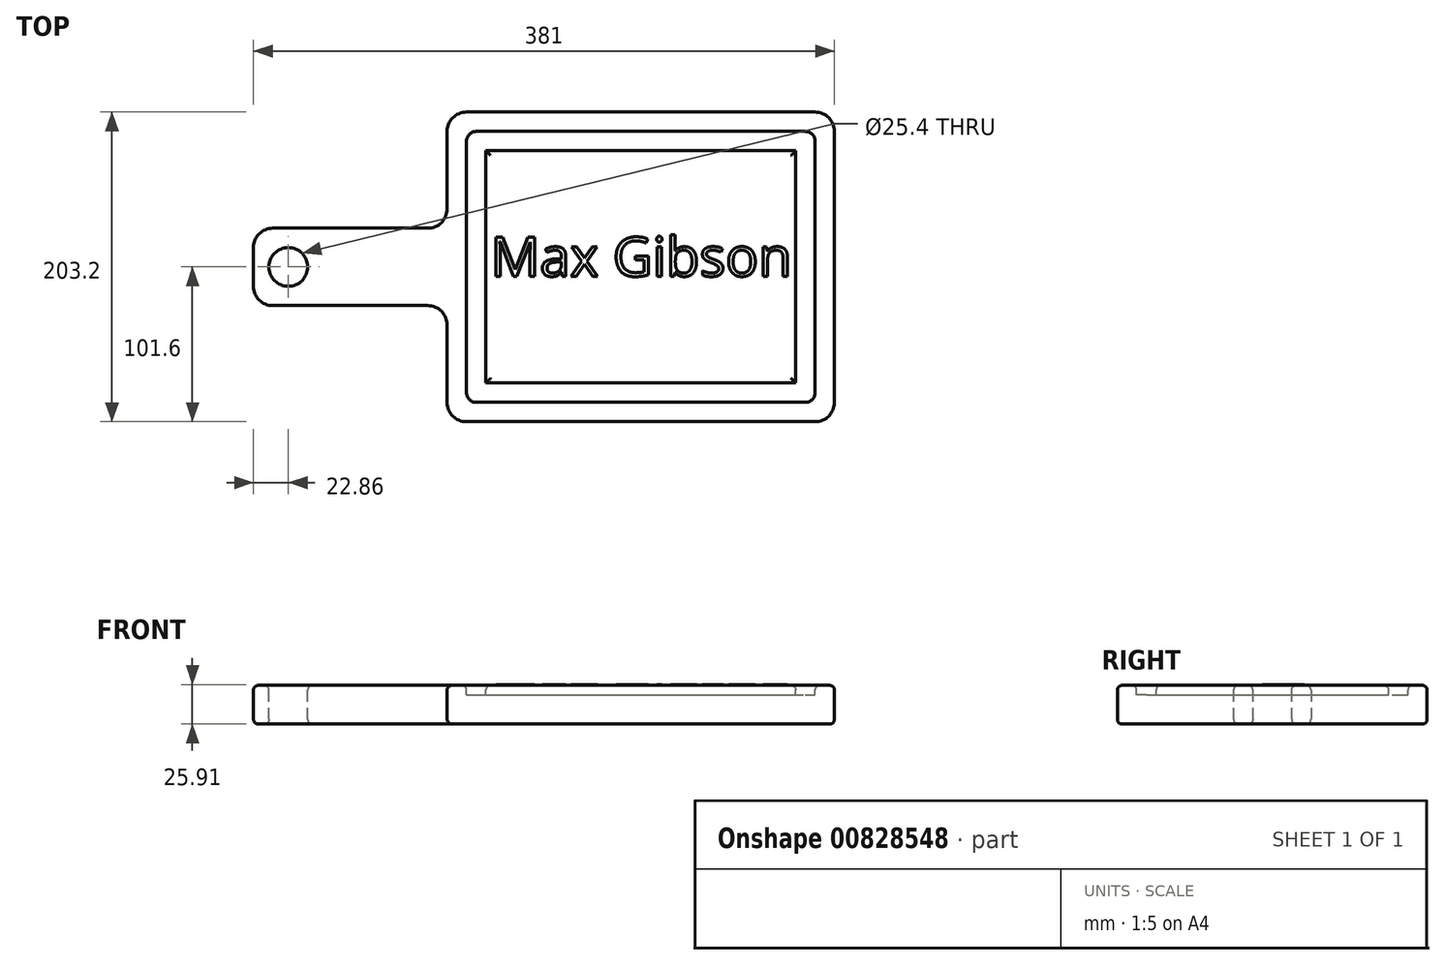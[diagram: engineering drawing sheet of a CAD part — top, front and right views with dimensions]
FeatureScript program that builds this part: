
annotation { "Feature Type Name" : "Feature", "Feature Type Description" : "" }
export const myFeature = defineFeature(function(context is Context, id is Id, definition is map)
    precondition{}
    {
        {
            var Q0;
            Q0=qCreatedBy(makeId("Top.planeOp"),FACE);
            var sketch = newSketch(context, id + "F0", { "sketchPlane" : qUnion([Q0])});
            skLineSegment(sketch, "E0.bottom", {"start": v(0, 0) * mm, "end": v(254, 0) * mm});
            skLineSegment(sketch, "E0.top", {"start": v(0, 203.2) * mm, "end": v(254, 203.2) * mm});
            skLineSegment(sketch, "E0.left", {"start": v(0, 0) * mm, "end": v(0, 203.2) * mm});
            skLineSegment(sketch, "E0.right", {"start": v(254, 0) * mm, "end": v(254, 203.2) * mm});
            skLineSegment(sketch, "E1.bottom", {"start": v(0, 127) * mm, "end": v(-127, 127) * mm});
            skLineSegment(sketch, "E1.top", {"start": v(0, 76.2) * mm, "end": v(-127, 76.2) * mm});
            skLineSegment(sketch, "E1.left", {"start": v(0, 127) * mm, "end": v(0, 76.2) * mm});
            skLineSegment(sketch, "E1.right", {"start": v(-127, 127) * mm, "end": v(-127, 76.2) * mm});
            skSolve(sketch);
        }
        {
            var Q0;
            {var subQ3=sQuery(id+"F0.wireOp",EDGE,"E0.bottom");Q0=makeQuery(id+"F0.imprint","IMPRINT",FACE,{"disambiguationData":[TD([[makeQuery(id+"F0.imprint","IMPRINT",EDGE,{"derivedFrom":subQ3}),1.0]])]});}
            var Q1;
            Q1=makeQuery(id+"F0.imprint","IMPRINT",FACE,{"disambiguationData":[TD([[makeQuery(id+"F0.imprint","IMPRINT",EDGE,{"derivedFrom":sQuery(id+"F0.wireOp",EDGE,"E1.bottom")}),1.0]])]});
            extrude(context, id + "F1", {"entities" : qUnion([Q0, Q1]), "depth" : 25.4 * mm, "offsetDistance" : 25.4 * mm});
        }
        {
            var Q0;
            Q0=makeQuery(id+"F1.opExtrude","CAP_FACE",FACE,{"disambiguationData":[OSD([sQuery(id+"F0.wireOp",EDGE,"E0.bottom"),sQuery(id+"F0.wireOp",EDGE,"E0.top"),sQuery(id+"F0.wireOp",EDGE,"E0.left"),sQuery(id+"F0.wireOp",EDGE,"E0.right"),sQuery(id+"F0.wireOp",EDGE,"E1.bottom"),sQuery(id+"F0.wireOp",EDGE,"E1.top"),sQuery(id+"F0.wireOp",EDGE,"E1.right")])],"isStart":false});
            var sketch = newSketch(context, id + "F2", { "sketchPlane" : qUnion([Q0])});
            skCircle(sketch, "E2", {"center": v(-104.14, 101.6) * mm, "radius": 12.7 * mm});
            skSolve(sketch);
        }
        {
            var Q0;
            Q0=makeQuery(id+"F2.imprint","IMPRINT",FACE,{"disambiguationData":[TD([[makeQuery(id+"F2.imprint","IMPRINT",EDGE,{"derivedFrom":sQuery(id+"F2.wireOp",EDGE,"E2")}),1.0]])]});
            extrude(context, id + "F3", {"entities" : qUnion([Q0]), "operationType" : NewBodyOperationType.REMOVE, "oppositeDirection" : true, "depth" : 25.4 * mm, "offsetDistance" : 25.4 * mm});
        }
        {
            var Q0;
            Q0=makeQuery(id+"F1.opExtrude","CAP_FACE",FACE,{"disambiguationData":[OSD([sQuery(id+"F0.wireOp",EDGE,"E0.bottom"),sQuery(id+"F0.wireOp",EDGE,"E0.top"),sQuery(id+"F0.wireOp",EDGE,"E0.left"),sQuery(id+"F0.wireOp",EDGE,"E0.right"),sQuery(id+"F0.wireOp",EDGE,"E1.bottom"),sQuery(id+"F0.wireOp",EDGE,"E1.top"),sQuery(id+"F0.wireOp",EDGE,"E1.right")])],"isStart":false});
            var sketch = newSketch(context, id + "F4", { "sketchPlane" : qUnion([Q0])});
            skLineSegment(sketch, "E3.0", {"start": v(12.7, 12.7) * mm, "end": v(12.7, 76.2) * mm});
            skLineSegment(sketch, "E3.1", {"start": v(12.7, 127) * mm, "end": v(12.7, 190.5) * mm});
            skLineSegment(sketch, "E3.2", {"start": v(12.7, 190.5) * mm, "end": v(241.3, 190.5) * mm});
            skLineSegment(sketch, "E3.3", {"start": v(241.3, 12.7) * mm, "end": v(241.3, 190.5) * mm});
            skLineSegment(sketch, "E3.4", {"start": v(12.7, 12.7) * mm, "end": v(241.3, 12.7) * mm});
            skLineSegment(sketch, "E4", {"start": v(12.7, 127) * mm, "end": v(12.7, 76.2) * mm});
            skLineSegment(sketch, "E5.0", {"start": v(25.4, 127) * mm, "end": v(25.4, 177.8) * mm});
            skLineSegment(sketch, "E5.1", {"start": v(228.6, 25.4) * mm, "end": v(228.6, 177.8) * mm});
            skLineSegment(sketch, "E5.2", {"start": v(25.4, 25.4) * mm, "end": v(228.6, 25.4) * mm});
            skLineSegment(sketch, "E5.3", {"start": v(25.4, 177.8) * mm, "end": v(228.6, 177.8) * mm});
            skLineSegment(sketch, "E5.4", {"start": v(25.4, 25.4) * mm, "end": v(25.4, 76.2) * mm});
            skLineSegment(sketch, "E5.5", {"start": v(25.4, 127) * mm, "end": v(25.4, 76.2) * mm});
            skSolve(sketch);
        }
        {
            var Q0;
            Q0=makeQuery(id+"F4.imprint","IMPRINT",FACE,{"disambiguationData":[TD([[makeQuery(id+"F4.imprint","IMPRINT",EDGE,{"derivedFrom":sQuery(id+"F4.wireOp",EDGE,"E3.0")}),-1.0]])]});
            extrude(context, id + "F5", {"entities" : qUnion([Q0]), "operationType" : NewBodyOperationType.REMOVE, "oppositeDirection" : true, "depth" : 6.35 * mm, "offsetDistance" : 25.4 * mm});
        }
        {
            var Q0;
            Q0=makeQuery(id+"F5.boolean.opBoolean","COPY",EDGE,{"derivedFrom":makeQuery(id+"F5.opExtrude","SWEPT_EDGE",EDGE,{"disambiguationData":[OSD([sQuery(id+"F4.wireOp",EDGE,"E3.1"),sQuery(id+"F4.wireOp",EDGE,"E3.2")])]})});
            var Q1;
            Q1=makeQuery(id+"F5.boolean.opBoolean","COPY",EDGE,{"derivedFrom":makeQuery(id+"F5.opExtrude","SWEPT_EDGE",EDGE,{"disambiguationData":[OSD([sQuery(id+"F4.wireOp",EDGE,"E3.2"),sQuery(id+"F4.wireOp",EDGE,"E3.3")])]})});
            var Q2;
            Q2=makeQuery(id+"F5.boolean.opBoolean","COPY",EDGE,{"derivedFrom":makeQuery(id+"F5.opExtrude","SWEPT_EDGE",EDGE,{"disambiguationData":[OSD([sQuery(id+"F4.wireOp",EDGE,"E3.3"),sQuery(id+"F4.wireOp",EDGE,"E3.4")])]})});
            var Q3;
            Q3=makeQuery(id+"F5.boolean.opBoolean","COPY",EDGE,{"derivedFrom":makeQuery(id+"F5.opExtrude","SWEPT_EDGE",EDGE,{"disambiguationData":[OSD([sQuery(id+"F4.wireOp",EDGE,"E3.0"),sQuery(id+"F4.wireOp",EDGE,"E3.4")])]})});
            fillet(context, id + "F6", {"entities" : qUnion([Q0, Q1, Q2, Q3]), "radius" : 6.35 * mm, "tangentPropagation" : true, "allowEdgeOverflow" : false});
        }
        {
            var Q0;
            Q0=makeQuery(id+"F1.opExtrude","SWEPT_EDGE",EDGE,{"disambiguationData":[OSD([sQuery(id+"F0.wireOp",EDGE,"E0.top"),sQuery(id+"F0.wireOp",EDGE,"E0.left")])]});
            var Q1;
            Q1=makeQuery(id+"F1.opExtrude","SWEPT_EDGE",EDGE,{"disambiguationData":[OSD([sQuery(id+"F0.wireOp",EDGE,"E1.bottom"),sQuery(id+"F0.wireOp",EDGE,"E1.right")])]});
            var Q2;
            Q2=makeQuery(id+"F1.opExtrude","SWEPT_EDGE",EDGE,{"disambiguationData":[OSD([sQuery(id+"F0.wireOp",EDGE,"E1.top"),sQuery(id+"F0.wireOp",EDGE,"E1.right")])]});
            var Q3;
            Q3=makeQuery(id+"F1.opExtrude","SWEPT_EDGE",EDGE,{"disambiguationData":[OSD([sQuery(id+"F0.wireOp",EDGE,"E0.bottom"),sQuery(id+"F0.wireOp",EDGE,"E0.left")])]});
            var Q4;
            Q4=makeQuery(id+"F1.opExtrude","SWEPT_EDGE",EDGE,{"disambiguationData":[OSD([sQuery(id+"F0.wireOp",EDGE,"E0.bottom"),sQuery(id+"F0.wireOp",EDGE,"E0.right")])]});
            var Q5;
            Q5=makeQuery(id+"F1.opExtrude","SWEPT_EDGE",EDGE,{"disambiguationData":[OSD([sQuery(id+"F0.wireOp",EDGE,"E0.top"),sQuery(id+"F0.wireOp",EDGE,"E0.right")])]});
            var Q6;
            Q6=makeQuery(id+"F1.opExtrude","SWEPT_EDGE",EDGE,{"disambiguationData":[OSD([sQuery(id+"F0.wireOp",EDGE,"E0.left"),sQuery(id+"F0.wireOp",EDGE,"E1.top"),sQuery(id+"F0.wireOp",EDGE,"E1.left")])]});
            var Q7;
            Q7=makeQuery(id+"F1.opExtrude","SWEPT_EDGE",EDGE,{"disambiguationData":[OSD([sQuery(id+"F0.wireOp",EDGE,"E0.left"),sQuery(id+"F0.wireOp",EDGE,"E1.bottom"),sQuery(id+"F0.wireOp",EDGE,"E1.left")])]});
            fillet(context, id + "F7", {"entities" : qUnion([Q0, Q1, Q2, Q3, Q4, Q5, Q6, Q7]), "radius" : 12.7 * mm, "tangentPropagation" : true, "allowEdgeOverflow" : false});
        }
        {
            var Q0;
            Q0=makeQuery(id+"F5.boolean.opBoolean","SPLIT",FACE,{"disambiguationData":[TD([makeQuery(id+"F5.opExtrude","SWEPT_FACE",FACE,{"disambiguationData":[OSD([sQuery(id+"F4.wireOp",EDGE,"E5.1")])]})])],"derivedFrom":makeQuery(id+"F1.opExtrude","CAP_FACE",FACE,{"disambiguationData":[OSD([sQuery(id+"F0.wireOp",EDGE,"E0.bottom"),sQuery(id+"F0.wireOp",EDGE,"E0.top"),sQuery(id+"F0.wireOp",EDGE,"E0.left"),sQuery(id+"F0.wireOp",EDGE,"E0.right"),sQuery(id+"F0.wireOp",EDGE,"E1.bottom"),sQuery(id+"F0.wireOp",EDGE,"E1.top"),sQuery(id+"F0.wireOp",EDGE,"E1.right")])],"isStart":false})});
            var Q1;
            {var subQ0=sQuery(id+"F0.wireOp",EDGE,"E0.left");var subQ1=sQuery(id+"F0.wireOp",EDGE,"E0.top");var subQ3=sQuery(id+"F0.wireOp",EDGE,"E1.bottom");var subQ4=sQuery(id+"F0.wireOp",EDGE,"E1.right");var subQ5=sQuery(id+"F0.wireOp",EDGE,"E1.top");var subQ6=sQuery(id+"F0.wireOp",EDGE,"E0.right");var subQ7=sQuery(id+"F0.wireOp",EDGE,"E0.bottom");Q1=makeQuery(id+"F5.boolean.opBoolean","SPLIT",FACE,{"disambiguationData":[TD([makeQuery(id+"F1.opExtrude","SWEPT_FACE",FACE,{"disambiguationData":[OSD([subQ7])]})])],"derivedFrom":makeQuery(id+"F1.opExtrude","CAP_FACE",FACE,{"disambiguationData":[OSD([subQ7,subQ1,subQ0,subQ6,subQ3,subQ5,subQ4])],"isStart":false})});}
            var Q2;
            Q2=makeQuery(id+"F1.opExtrude","CAP_FACE",FACE,{"disambiguationData":[OSD([sQuery(id+"F0.wireOp",EDGE,"E0.bottom"),sQuery(id+"F0.wireOp",EDGE,"E0.top"),sQuery(id+"F0.wireOp",EDGE,"E0.left"),sQuery(id+"F0.wireOp",EDGE,"E0.right"),sQuery(id+"F0.wireOp",EDGE,"E1.bottom"),sQuery(id+"F0.wireOp",EDGE,"E1.top"),sQuery(id+"F0.wireOp",EDGE,"E1.right")])],"isStart":true});
            fillet(context, id + "F8", {"entities" : qUnion([Q0, Q1, Q2]), "radius" : 3.17 * mm, "tangentPropagation" : true, "allowEdgeOverflow" : false});
        }
        {
            var Q0;
            Q0=makeQuery(id+"F5.boolean.opBoolean","SPLIT",FACE,{"disambiguationData":[TD([makeQuery(id+"F5.opExtrude","SWEPT_FACE",FACE,{"disambiguationData":[OSD([sQuery(id+"F4.wireOp",EDGE,"E5.1")])]})])],"derivedFrom":makeQuery(id+"F1.opExtrude","CAP_FACE",FACE,{"disambiguationData":[OSD([sQuery(id+"F0.wireOp",EDGE,"E0.bottom"),sQuery(id+"F0.wireOp",EDGE,"E0.top"),sQuery(id+"F0.wireOp",EDGE,"E0.left"),sQuery(id+"F0.wireOp",EDGE,"E0.right"),sQuery(id+"F0.wireOp",EDGE,"E1.bottom"),sQuery(id+"F0.wireOp",EDGE,"E1.top"),sQuery(id+"F0.wireOp",EDGE,"E1.right")])],"isStart":false})});
            var sketch = newSketch(context, id + "F9", { "sketchPlane" : qUnion([Q0])});
            skText(sketch, "E6", { "text": "Max Gibson", "fontName": "OpenSans-Regular.ttf"});
            const initialGuessF9  = {"E6": [0.02858, 0.09552, 1, 0, 0.0257]};
            skSetInitialGuess(sketch, initialGuessF9);
            skSolve(sketch);
        }
        {
            var Q0;
            Q0 = qSketchRegion(id + "F9", true);
            extrude(context, id + "F10", {"entities" : qUnion([Q0]), "operationType" : NewBodyOperationType.ADD, "depth" : 0.5 * mm, "offsetDistance" : 25.4 * mm});
        }
    });
